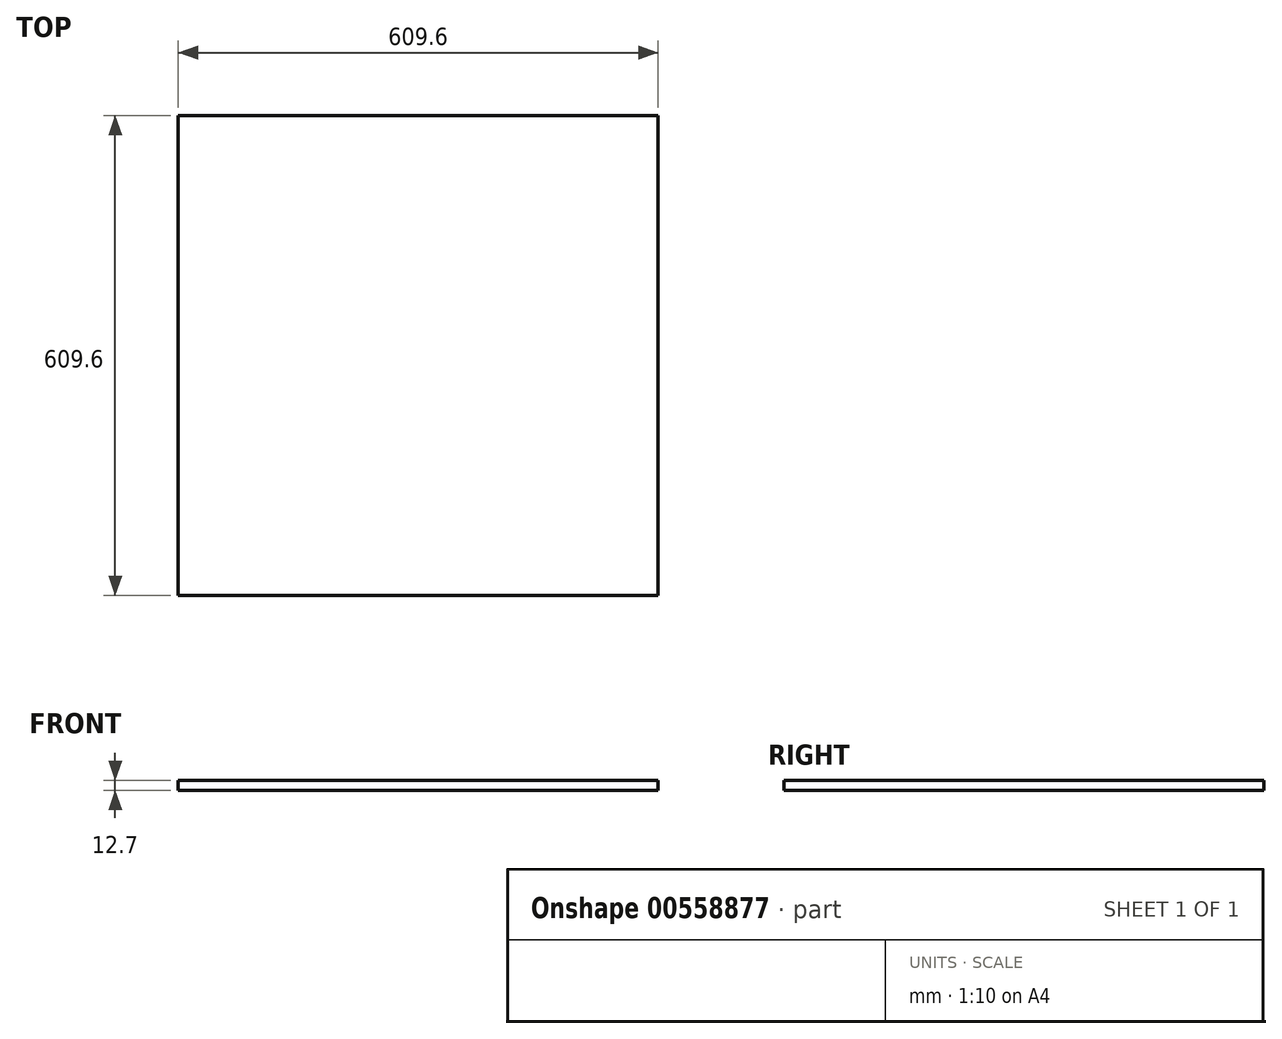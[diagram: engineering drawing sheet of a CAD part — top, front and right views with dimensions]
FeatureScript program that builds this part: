
annotation { "Feature Type Name" : "Feature", "Feature Type Description" : "" }
export const myFeature = defineFeature(function(context is Context, id is Id, definition is map)
    precondition{}
    {
        {
            var Q0;
            Q0=qCreatedBy(makeId("Top.planeOp"),FACE);
            var sketch = newSketch(context, id + "F0", { "sketchPlane" : qUnion([Q0])});
            skLineSegment(sketch, "E0.bottom", {"start": v(-305.08, 329.39) * mm, "end": v(304.52, 329.39) * mm});
            skLineSegment(sketch, "E0.top", {"start": v(-305.08, -280.21) * mm, "end": v(304.52, -280.21) * mm});
            skLineSegment(sketch, "E0.left", {"start": v(-305.08, 329.39) * mm, "end": v(-305.08, -280.21) * mm});
            skLineSegment(sketch, "E0.right", {"start": v(304.52, 329.39) * mm, "end": v(304.52, -280.21) * mm});
            skSolve(sketch);
        }
        {
            var Q0;
            Q0 = qSketchRegion(id + "F0", true);
            extrude(context, id + "F1", {"entities" : qUnion([Q0]), "depth" : 12.7 * mm, "offsetDistance" : 25.4 * mm});
        }
    });
